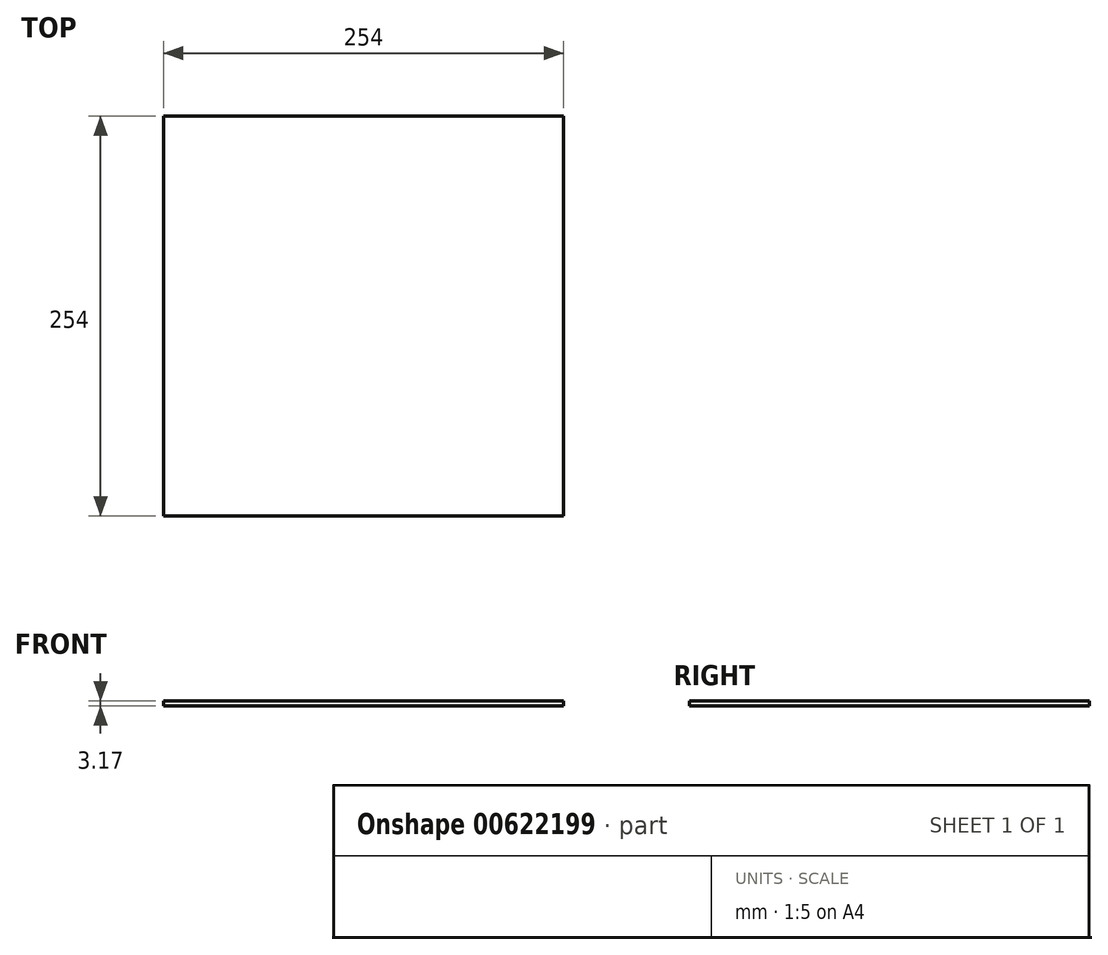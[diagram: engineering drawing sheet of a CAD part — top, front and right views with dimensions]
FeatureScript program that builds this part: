
annotation { "Feature Type Name" : "Feature", "Feature Type Description" : "" }
export const myFeature = defineFeature(function(context is Context, id is Id, definition is map)
    precondition{}
    {
        {
            var Q0;
            Q0=qCreatedBy(makeId("Top.planeOp"),FACE);
            var sketch = newSketch(context, id + "F0", { "sketchPlane" : qUnion([Q0])});
            skLineSegment(sketch, "E0.bottom", {"start": v(0, 0) * mm, "end": v(254, 0) * mm});
            skLineSegment(sketch, "E0.top", {"start": v(0, 254) * mm, "end": v(254, 254) * mm});
            skLineSegment(sketch, "E0.left", {"start": v(0, 0) * mm, "end": v(0, 254) * mm});
            skLineSegment(sketch, "E0.right", {"start": v(254, 0) * mm, "end": v(254, 254) * mm});
            skSolve(sketch);
        }
        {
            var Q0;
            Q0 = qSketchRegion(id + "F0", true);
            extrude(context, id + "F1", {"entities" : qUnion([Q0]), "depth" : 3.17 * mm, "offsetDistance" : 25.4 * mm});
        }
    });
